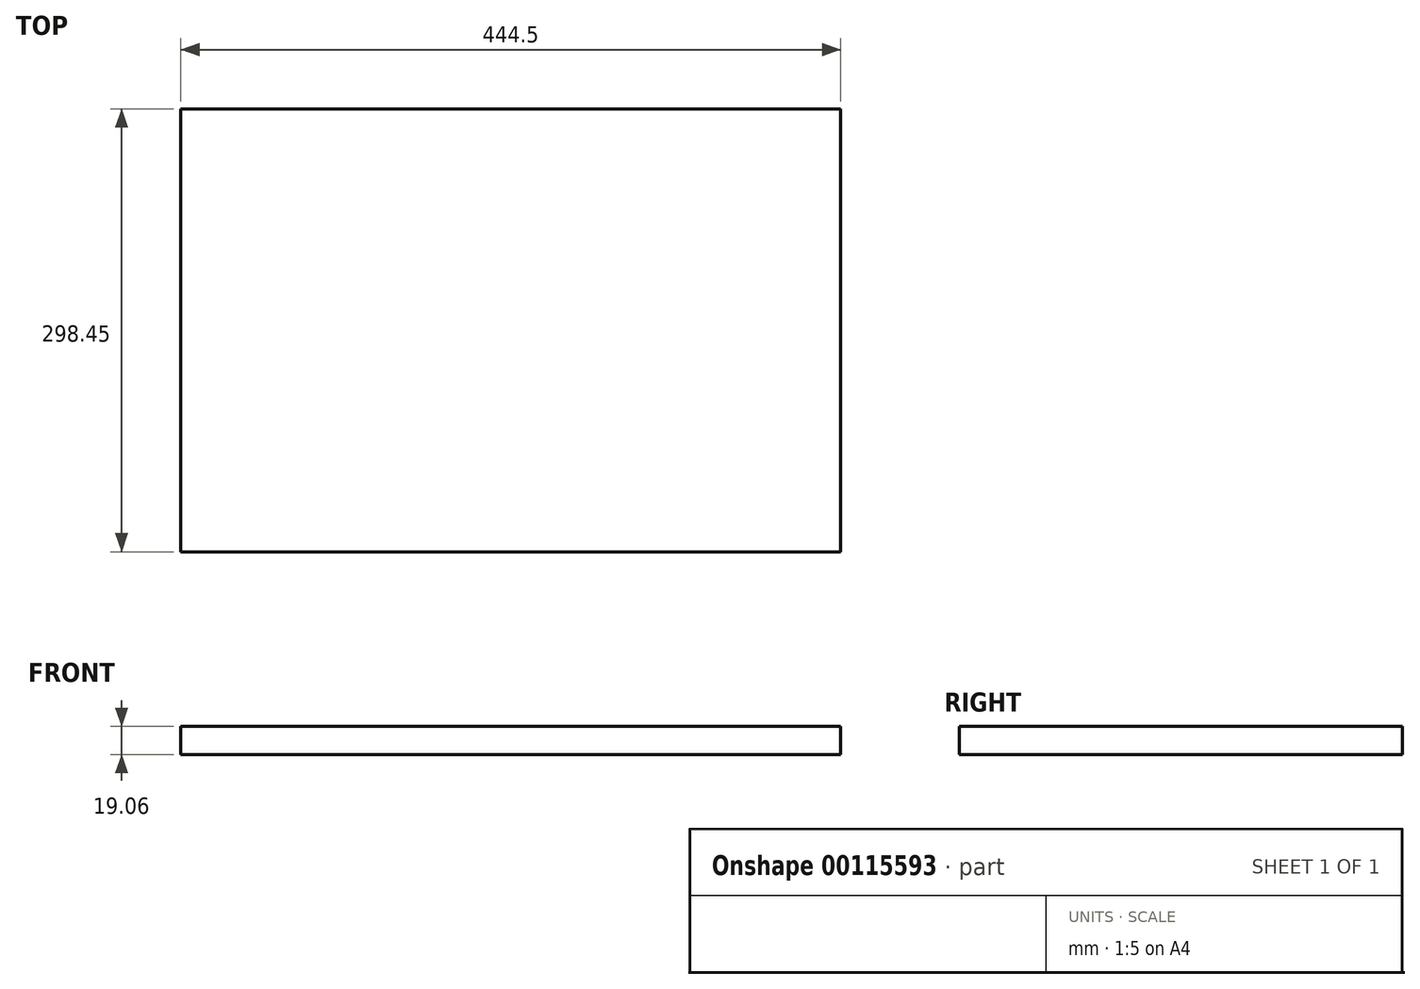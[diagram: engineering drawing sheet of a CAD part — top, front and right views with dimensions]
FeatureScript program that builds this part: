
annotation { "Feature Type Name" : "Feature", "Feature Type Description" : "" }
export const myFeature = defineFeature(function(context is Context, id is Id, definition is map)
    precondition{}
    {
        {
            var Q0;
            Q0=qCreatedBy(makeId("Front.planeOp"),FACE);
            var sketch = newSketch(context, id + "F0", { "sketchPlane" : qUnion([Q0])});
            skLineSegment(sketch, "E0.bottom", {"start": v(-222.25, 9.53) * mm, "end": v(222.25, 9.53) * mm});
            skLineSegment(sketch, "E0.top", {"start": v(-222.25, -9.53) * mm, "end": v(222.25, -9.53) * mm});
            skLineSegment(sketch, "E0.left", {"start": v(-222.25, 9.53) * mm, "end": v(-222.25, -9.52) * mm});
            skLineSegment(sketch, "E0.right", {"start": v(222.25, 9.53) * mm, "end": v(222.25, -9.52) * mm});
            skPoint(sketch, "E0.middle", {"position": v(0, 0) * mm});
            skSolve(sketch);
        }
        {
            var Q0;
            Q0=makeQuery(id+"F0.imprint","IMPRINT",FACE,{"disambiguationData":[TD([[makeQuery(id+"F0.imprint","IMPRINT",EDGE,{"derivedFrom":sQuery(id+"F0.wireOp",EDGE,"E0.bottom")}),-1.0]])]});
            extrude(context, id + "F1", {"entities" : qUnion([Q0]), "depth" : 298.45 * mm});
        }
    });
